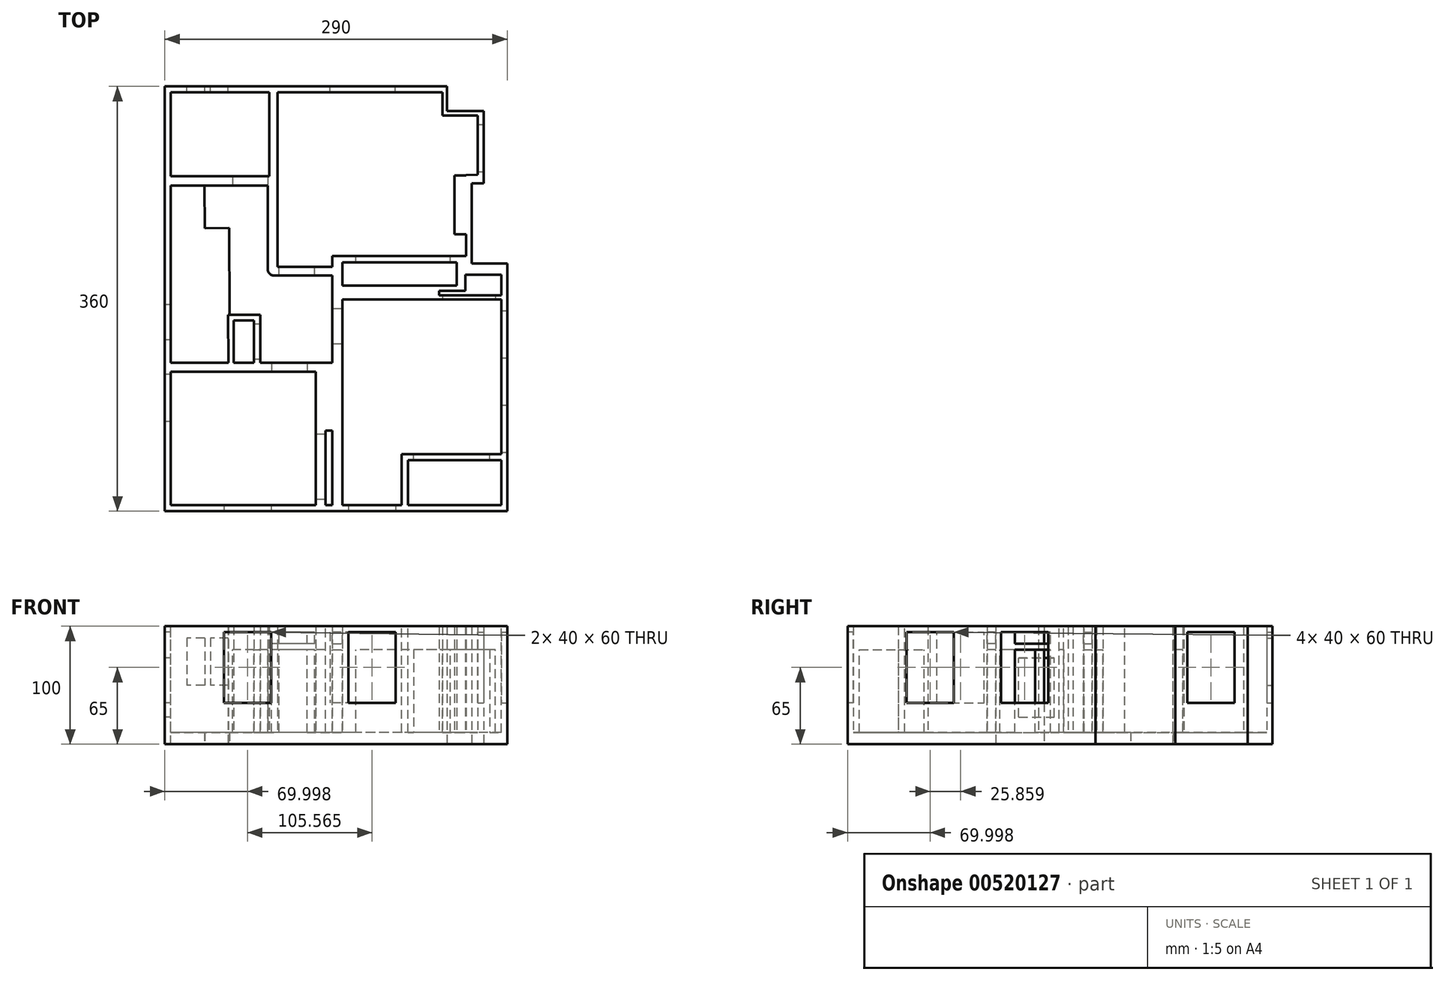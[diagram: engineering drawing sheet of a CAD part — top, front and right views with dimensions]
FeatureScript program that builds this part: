
annotation { "Feature Type Name" : "Feature", "Feature Type Description" : "" }
export const myFeature = defineFeature(function(context is Context, id is Id, definition is map)
    precondition{}
    {
        {
            var Q0;
            Q0=qCreatedBy(makeId("Top.planeOp"),FACE);
            var sketch = newSketch(context, id + "F0", { "sketchPlane" : qUnion([Q0])});
            skLineSegment(sketch, "E0.bottom", {"start": v(-136.75, 209.7) * mm, "end": v(93.5, 209.7) * mm});
            skLineSegment(sketch, "E0.top", {"start": v(-136.75, -140.3) * mm, "end": v(0, -140.3) * mm});
            skLineSegment(sketch, "E0.left", {"start": v(-136.75, 209.7) * mm, "end": v(-136.75, -20.3) * mm});
            skLineSegment(sketch, "E0.right", {"start": v(143.25, 59.7) * mm, "end": v(143.25, -140.3) * mm});
            skLineSegment(sketch, "E1", {"start": v(113.25, 59.7) * mm, "end": v(143.25, 59.7) * mm});
            skLineSegment(sketch, "E2", {"start": v(103.25, 89.37) * mm, "end": v(103.25, 139.37) * mm});
            skLineSegment(sketch, "E3", {"start": v(123.25, 139.7) * mm, "end": v(123.25, 190.05) * mm});
            skLineSegment(sketch, "E4", {"start": v(103.25, 139.37) * mm, "end": v(123.25, 139.7) * mm});
            skLineSegment(sketch, "E5", {"start": v(113.25, 59.7) * mm, "end": v(113.25, 139.54) * mm});
            skLineSegment(sketch, "E6", {"start": v(3.25, -140.3) * mm, "end": v(3.25, 69.7) * mm});
            skLineSegment(sketch, "E7", {"start": v(3.25, 69.7) * mm, "end": v(113.25, 69.7) * mm});
            skLineSegment(sketch, "E8", {"start": v(3.25, 39.7) * mm, "end": v(143.25, 39.7) * mm});
            skLineSegment(sketch, "E9", {"start": v(63.25, 69.7) * mm, "end": v(63.25, 39.7) * mm});
            skLineSegment(sketch, "E10", {"start": v(3.25, -20.3) * mm, "end": v(-136.75, -20.3) * mm});
            skLineSegment(sketch, "E11", {"start": v(-46.75, 59.7) * mm, "end": v(-46.75, 209.7) * mm});
            skLineSegment(sketch, "E12", {"start": v(-46.75, 59.7) * mm, "end": v(3.25, 59.7) * mm});
            skLineSegment(sketch, "E13", {"start": v(-136.75, 129.7) * mm, "end": v(-46.75, 129.7) * mm});
            skLineSegment(sketch, "E14", {"start": v(103.25, 89.37) * mm, "end": v(113.25, 89.37) * mm});
            skLineSegment(sketch, "E15", {"start": v(-80.56, 99.7) * mm, "end": v(-80.56, -20.3) * mm});
            skLineSegment(sketch, "E16", {"start": v(-80.56, 99.7) * mm, "end": v(-136.75, 99.7) * mm});
            skLineSegment(sketch, "E17", {"start": v(-141.75, 214.7) * mm, "end": v(-141.75, -145.77) * mm});
            skLineSegment(sketch, "E18", {"start": v(-141.75, -145.3) * mm, "end": v(148.25, -145.3) * mm});
            skLineSegment(sketch, "E19", {"start": v(148.25, -145.3) * mm, "end": v(148.25, 64.7) * mm});
            skLineSegment(sketch, "E20", {"start": v(148.25, 64.7) * mm, "end": v(118.25, 64.7) * mm});
            skLineSegment(sketch, "E21", {"start": v(118.25, 64.7) * mm, "end": v(118.25, 132.41) * mm});
            skLineSegment(sketch, "E22", {"start": v(118.25, 132.41) * mm, "end": v(128.25, 132.41) * mm});
            skLineSegment(sketch, "E23", {"start": v(128.25, 132.41) * mm, "end": v(128.25, 193.74) * mm});
            skLineSegment(sketch, "E24", {"start": v(97.29, 214.7) * mm, "end": v(-141.75, 214.7) * mm});
            skLineSegment(sketch, "E25", {"start": v(-136.75, 135.4) * mm, "end": v(-52.51, 135.4) * mm});
            skLineSegment(sketch, "E26", {"start": v(-52.51, 135.4) * mm, "end": v(-52.51, 209.7) * mm});
            skLineSegment(sketch, "E27", {"start": v(-53.07, 129.7) * mm, "end": v(-53.07, 59.7) * mm});
            skLineSegment(sketch, "E28", {"start": v(-53.07, 59.7) * mm, "end": v(-53.07, 54.34) * mm});
            skLineSegment(sketch, "E29", {"start": v(-53.07, 54.34) * mm, "end": v(3.25, 54.34) * mm});
            skLineSegment(sketch, "E30.bottom", {"start": v(5.65, 66.66) * mm, "end": v(60.34, 66.66) * mm});
            skLineSegment(sketch, "E30.top", {"start": v(5.65, 42.9) * mm, "end": v(60.34, 42.9) * mm});
            skLineSegment(sketch, "E30.left", {"start": v(5.65, 66.66) * mm, "end": v(5.65, 42.9) * mm});
            skLineSegment(sketch, "E30.right", {"start": v(60.34, 66.66) * mm, "end": v(60.34, 42.9) * mm});
            skLineSegment(sketch, "E31.bottom", {"start": v(-136.75, -24.43) * mm, "end": v(0, -24.43) * mm});
            skLineSegment(sketch, "E31.left", {"start": v(-136.75, -24.43) * mm, "end": v(-136.75, -140.3) * mm});
            skLineSegment(sketch, "E31.right", {"start": v(0, -24.43) * mm, "end": v(0, -134.7) * mm});
            skLineSegment(sketch, "E32.bottom", {"start": v(7.81, 34.85) * mm, "end": v(138.07, 34.85) * mm});
            skLineSegment(sketch, "E32.top", {"start": v(7.81, -134.7) * mm, "end": v(138.07, -134.7) * mm});
            skLineSegment(sketch, "E32.left", {"start": v(7.81, 34.85) * mm, "end": v(7.81, -134.7) * mm});
            skLineSegment(sketch, "E32.right", {"start": v(138.07, 34.85) * mm, "end": v(138.07, -134.7) * mm});
            skLineSegment(sketch, "E33", {"start": v(67.33, 44.96) * mm, "end": v(67.33, 65.85) * mm});
            skLineSegment(sketch, "E34", {"start": v(67.33, 65.85) * mm, "end": v(108.15, 65.85) * mm});
            skLineSegment(sketch, "E35", {"start": v(108.15, 65.85) * mm, "end": v(108.15, 55.21) * mm});
            skLineSegment(sketch, "E36", {"start": v(108.15, 55.21) * mm, "end": v(138.12, 55.21) * mm});
            skLineSegment(sketch, "E37", {"start": v(138.12, 55.21) * mm, "end": v(138.12, 44.96) * mm});
            skLineSegment(sketch, "E38", {"start": v(138.12, 44.96) * mm, "end": v(67.33, 44.96) * mm});
            skLineSegment(sketch, "E39", {"start": v(-136.75, 94.77) * mm, "end": v(-86.74, 94.77) * mm});
            skLineSegment(sketch, "E40", {"start": v(-86.74, 94.77) * mm, "end": v(-86.74, -20.3) * mm});
            skLineSegment(sketch, "E41", {"start": v(97.29, 214.7) * mm, "end": v(97.29, 193.74) * mm});
            skLineSegment(sketch, "E42", {"start": v(97.29, 193.74) * mm, "end": v(128.25, 193.74) * mm});
            skLineSegment(sketch, "E43", {"start": v(128.25, 193.74) * mm, "end": v(128.25, 190.05) * mm});
            skLineSegment(sketch, "E44", {"start": v(123.25, 190.05) * mm, "end": v(93.5, 190.05) * mm});
            skLineSegment(sketch, "E45", {"start": v(93.5, 190.05) * mm, "end": v(93.5, 209.7) * mm});
            skPoint(sketch, "E46.orphan", {"position": v(123.25, 209.7) * mm});
            skLineSegment(sketch, "E47", {"start": v(0, -134.7) * mm, "end": v(0, -140.3) * mm});
            skLineSegment(sketch, "E48.trimOffspring", {"start": v(3.25, -140.3) * mm, "end": v(143.25, -140.3) * mm});
            skSolve(sketch);
        }
        {
            var Q0;
            Q0=qCreatedBy(makeId("Top.planeOp"),FACE);
            var sketch = newSketch(context, id + "F1", { "sketchPlane" : qUnion([Q0])});
            skLineSegment(sketch, "E49", {"start": v(-53.18, 210.11) * mm, "end": v(-53.18, 138.73) * mm});
            skLineSegment(sketch, "E50", {"start": v(-53.18, 138.73) * mm, "end": v(-138.25, 138.73) * mm});
            skLineSegment(sketch, "E51", {"start": v(-138.25, 138.73) * mm, "end": v(-138.25, 130.57) * mm});
            skLineSegment(sketch, "E52", {"start": v(-138.25, 130.57) * mm, "end": v(-54.54, 130.57) * mm});
            skLineSegment(sketch, "E53", {"start": v(-54.54, 130.57) * mm, "end": v(-54.54, 54.42) * mm});
            skLineSegment(sketch, "E54", {"start": v(-54.54, 54.42) * mm, "end": v(0, 54.42) * mm});
            skLineSegment(sketch, "E55", {"start": v(0, 54.42) * mm, "end": v(0, -19.68) * mm});
            skLineSegment(sketch, "E56", {"start": v(0, -19.68) * mm, "end": v(-61, -19.68) * mm});
            skLineSegment(sketch, "E57", {"start": v(-137.2, -27.08) * mm, "end": v(-13.82, -27.08) * mm});
            skLineSegment(sketch, "E58", {"start": v(0, -143.06) * mm, "end": v(8.69, -143.06) * mm});
            skLineSegment(sketch, "E59", {"start": v(8.69, -143.06) * mm, "end": v(8.69, 34.03) * mm});
            skLineSegment(sketch, "E60", {"start": v(8.77, 45.73) * mm, "end": v(8.77, 65.56) * mm});
            skLineSegment(sketch, "E61", {"start": v(8.77, 65.56) * mm, "end": v(105.55, 65.56) * mm});
            skLineSegment(sketch, "E62", {"start": v(105.55, 65.56) * mm, "end": v(105.55, 55.1) * mm});
            skLineSegment(sketch, "E63", {"start": v(112.8, 55.1) * mm, "end": v(143.3, 55.1) * mm});
            skLineSegment(sketch, "E64", {"start": v(90.95, 65.56) * mm, "end": v(96.31, 65.56) * mm});
            skLineSegment(sketch, "E65", {"start": v(-53.18, 210.11) * mm, "end": v(-46.38, 210.11) * mm});
            skLineSegment(sketch, "E66", {"start": v(-46.38, 210.11) * mm, "end": v(-46.38, 61.89) * mm});
            skLineSegment(sketch, "E67", {"start": v(-46.38, 61.89) * mm, "end": v(0, 61.89) * mm});
            skLineSegment(sketch, "E68", {"start": v(0, 61.89) * mm, "end": v(0, 71.07) * mm});
            skLineSegment(sketch, "E69", {"start": v(0, 71.07) * mm, "end": v(114.87, 71.07) * mm});
            skLineSegment(sketch, "E70", {"start": v(114.87, 71.07) * mm, "end": v(114.87, 61.89) * mm});
            skLineSegment(sketch, "E71", {"start": v(114.87, 61.89) * mm, "end": v(144.27, 61.89) * mm});
            skLineSegment(sketch, "E72", {"start": v(144.27, 61.89) * mm, "end": v(143.3, 55.1) * mm});
            skLineSegment(sketch, "E73", {"start": v(113.41, 89.48) * mm, "end": v(103.62, 89.48) * mm});
            skLineSegment(sketch, "E74", {"start": v(103.62, 89.48) * mm, "end": v(103.62, 139.21) * mm});
            skLineSegment(sketch, "E75", {"start": v(103.62, 139.21) * mm, "end": v(113.8, 139.21) * mm});
            skLineSegment(sketch, "E76", {"start": v(113.8, 139.21) * mm, "end": v(113.41, 89.48) * mm});
            skLineSegment(sketch, "E77", {"start": v(-87.85, -19.68) * mm, "end": v(-137.24, -19.68) * mm});
            skLineSegment(sketch, "E78", {"start": v(-137.24, -19.68) * mm, "end": v(-137.2, -27.08) * mm});
            skLineSegment(sketch, "E79", {"start": v(138, 55.1) * mm, "end": v(143.3, 55.1) * mm});
            skLineSegment(sketch, "E80", {"start": v(105.55, 55.1) * mm, "end": v(105.55, 45.73) * mm});
            skLineSegment(sketch, "E81", {"start": v(8.77, 45.73) * mm, "end": v(105.55, 45.73) * mm});
            skLineSegment(sketch, "E82", {"start": v(8.69, 34.03) * mm, "end": v(90.67, 34.03) * mm});
            skLineSegment(sketch, "E83", {"start": v(90.67, 37.73) * mm, "end": v(90.67, 41.44) * mm});
            skLineSegment(sketch, "E84", {"start": v(90.67, 41.44) * mm, "end": v(112.8, 41.44) * mm});
            skLineSegment(sketch, "E85", {"start": v(112.8, 41.44) * mm, "end": v(112.8, 55.1) * mm});
            skLineSegment(sketch, "E86", {"start": v(112.8, 55.1) * mm, "end": v(112.8, 55.1) * mm});
            skPoint(sketch, "E87.orphan", {"position": v(0, -27.08) * mm});
            skLineSegment(sketch, "E88", {"start": v(-13.82, -27.08) * mm, "end": v(-13.82, -77.07) * mm});
            skLineSegment(sketch, "E89", {"start": v(-5.52, -77.07) * mm, "end": v(0, -77.07) * mm});
            skLineSegment(sketch, "E90", {"start": v(0, -77.07) * mm, "end": v(0, -143.06) * mm});
            skLineSegment(sketch, "E91", {"start": v(90.67, 34.03) * mm, "end": v(145.65, 34.03) * mm});
            skLineSegment(sketch, "E92", {"start": v(90.67, 37.73) * mm, "end": v(145.65, 37.73) * mm});
            skLineSegment(sketch, "E93", {"start": v(145.65, 37.73) * mm, "end": v(145.65, 34.03) * mm});
            skLineSegment(sketch, "E94", {"start": v(-13.82, -77.07) * mm, "end": v(-13.82, -142.7) * mm});
            skLineSegment(sketch, "E95", {"start": v(-13.82, -142.7) * mm, "end": v(-5.52, -142.7) * mm});
            skLineSegment(sketch, "E96", {"start": v(-5.52, -142.7) * mm, "end": v(-5.52, -77.07) * mm});
            skLineSegment(sketch, "E97", {"start": v(58.82, -141.74) * mm, "end": v(58.82, -96.98) * mm});
            skLineSegment(sketch, "E98", {"start": v(58.82, -96.98) * mm, "end": v(144.68, -96.98) * mm});
            skLineSegment(sketch, "E99", {"start": v(64.28, -141.74) * mm, "end": v(64.28, -102.13) * mm});
            skLineSegment(sketch, "E100", {"start": v(58.82, -141.74) * mm, "end": v(64.28, -141.74) * mm});
            skLineSegment(sketch, "E101", {"start": v(144.68, -96.98) * mm, "end": v(144.68, -102.13) * mm});
            skLineSegment(sketch, "E102", {"start": v(144.68, -102.13) * mm, "end": v(64.28, -102.13) * mm});
            skLineSegment(sketch, "E103.bottom", {"start": v(93.55, 212.13) * mm, "end": v(97.19, 212.13) * mm});
            skLineSegment(sketch, "E103.top", {"start": v(93.55, 190.13) * mm, "end": v(124.8, 190.13) * mm});
            skLineSegment(sketch, "E103.left", {"start": v(93.55, 212.13) * mm, "end": v(93.55, 190.13) * mm});
            skLineSegment(sketch, "E103.right", {"start": v(124.8, 193.53) * mm, "end": v(124.8, 190.13) * mm});
            skLineSegment(sketch, "E104", {"start": v(97.19, 212.13) * mm, "end": v(97.19, 193.53) * mm});
            skLineSegment(sketch, "E105", {"start": v(97.19, 193.53) * mm, "end": v(124.8, 193.53) * mm});
            skLineSegment(sketch, "E106", {"start": v(-61, -19.68) * mm, "end": v(-61, 21.1) * mm});
            skLineSegment(sketch, "E107", {"start": v(-61, 21.1) * mm, "end": v(-88.21, 21.1) * mm});
            skLineSegment(sketch, "E108", {"start": v(-88.21, 21.1) * mm, "end": v(-87.85, -19.68) * mm});
            skLineSegment(sketch, "E109.bottom", {"start": v(-83.58, 16.47) * mm, "end": v(-66.22, 16.47) * mm});
            skLineSegment(sketch, "E109.top", {"start": v(-83.58, -19.68) * mm, "end": v(-66.22, -19.68) * mm});
            skLineSegment(sketch, "E109.left", {"start": v(-83.58, 16.47) * mm, "end": v(-83.58, -19.68) * mm});
            skLineSegment(sketch, "E109.right", {"start": v(-66.22, 16.47) * mm, "end": v(-66.22, -19.68) * mm});
            skSolve(sketch);
        }
        {
            var Q0;
            Q0=qCreatedBy(makeId("Top.planeOp"),FACE);
            var sketch = newSketch(context, id + "F2", { "sketchPlane" : qUnion([Q0])});
            skLineSegment(sketch, "E110", {"start": v(-138.73, 211.72) * mm, "end": v(95.24, 211.72) * mm});
            skLineSegment(sketch, "E111", {"start": v(124.93, 192.2) * mm, "end": v(124.93, 138.77) * mm});
            skLineSegment(sketch, "E112", {"start": v(124.93, 138.77) * mm, "end": v(113.56, 138.77) * mm});
            skLineSegment(sketch, "E113", {"start": v(113.56, 138.77) * mm, "end": v(113.56, 61.87) * mm});
            skLineSegment(sketch, "E114", {"start": v(113.56, 61.87) * mm, "end": v(144.48, 61.87) * mm});
            skLineSegment(sketch, "E115", {"start": v(144.48, 61.87) * mm, "end": v(144.48, -142.02) * mm});
            skLineSegment(sketch, "E116", {"start": v(144.48, -142.02) * mm, "end": v(-137.63, -142.02) * mm});
            skLineSegment(sketch, "E117", {"start": v(-137.3, -85.55) * mm, "end": v(-137.61, -19.93) * mm});
            skLineSegment(sketch, "E118", {"start": v(-87.17, 94.65) * mm, "end": v(-86.91, -19.68) * mm});
            skLineSegment(sketch, "E119", {"start": v(-86.91, -19.68) * mm, "end": v(-137.61, -19.93) * mm});
            skLineSegment(sketch, "E120.trimOffspring", {"start": v(-138.34, 131.48) * mm, "end": v(-138.73, 211.72) * mm});
            skLineSegment(sketch, "E121", {"start": v(-87.17, 94.65) * mm, "end": v(-108.05, 94.6) * mm});
            skLineSegment(sketch, "E122", {"start": v(-108.05, 94.6) * mm, "end": v(-108.13, 131.48) * mm});
            skLineSegment(sketch, "E123", {"start": v(-108.13, 131.48) * mm, "end": v(-138.34, 131.48) * mm});
            skLineSegment(sketch, "E124", {"start": v(-137.9, -85.55) * mm, "end": v(-137.3, -85.55) * mm});
            skLineSegment(sketch, "E125", {"start": v(-137.9, -85.55) * mm, "end": v(-137.63, -142.02) * mm});
            skLineSegment(sketch, "E126", {"start": v(95.24, 211.72) * mm, "end": v(95.24, 192.2) * mm});
            skLineSegment(sketch, "E127", {"start": v(95.24, 192.2) * mm, "end": v(124.93, 192.2) * mm});
            skSolve(sketch);
        }
        {
            var Q0;
            Q0 = qSketchRegion(id + "F2", true);
            extrude(context, id + "F3", {"entities" : qUnion([Q0]), "depth" : 10 * mm, "offsetDistance" : 25 * mm});
        }
        {
            var Q0;
            Q0 = qSketchRegion(id + "F0", true);
            extrude(context, id + "F4", {"entities" : qUnion([Q0]), "operationType" : NewBodyOperationType.ADD, "depth" : 100 * mm, "offsetDistance" : 25 * mm});
        }
        {
            var Q0;
            Q0 = qSketchRegion(id + "F1", true);
            extrude(context, id + "F5", {"entities" : qUnion([Q0]), "operationType" : NewBodyOperationType.ADD, "depth" : 100 * mm, "offsetDistance" : 25 * mm});
        }
        {
            var Q0;
            Q0=makeQuery(id+"F4.opExtrude","SWEPT_FACE",FACE,{"disambiguationData":[OSD([sQuery(id+"F0.wireOp",EDGE,"E19")])]});
            var sketch = newSketch(context, id + "F6", { "sketchPlane" : qUnion([Q0])});
            skPoint(sketch, "E128.oppositeSnap0", {"position": v(-19.27, 35) * mm});
            skLineSegment(sketch, "E128.bottom", {"start": v(-95.3, 95) * mm, "end": v(-55.3, 95) * mm});
            skLineSegment(sketch, "E128.top", {"start": v(-95.3, 35) * mm, "end": v(-55.3, 35) * mm});
            skLineSegment(sketch, "E128.left", {"start": v(-95.3, 95) * mm, "end": v(-95.3, 35) * mm});
            skLineSegment(sketch, "E128.right", {"start": v(-55.3, 95) * mm, "end": v(-55.3, 35) * mm});
            skLineSegment(sketch, "E129.bottom", {"start": v(-15.3, 95) * mm, "end": v(24.7, 95) * mm});
            skLineSegment(sketch, "E129.top", {"start": v(-15.3, 35) * mm, "end": v(24.7, 35) * mm});
            skLineSegment(sketch, "E129.left", {"start": v(-15.3, 95) * mm, "end": v(-15.3, 35) * mm});
            skLineSegment(sketch, "E129.right", {"start": v(24.7, 95) * mm, "end": v(24.7, 35) * mm});
            skSolve(sketch);
        }
        {
            var Q0;
            Q0 = qSketchRegion(id + "F6", true);
            extrude(context, id + "F7", {"entities" : qUnion([Q0]), "operationType" : NewBodyOperationType.REMOVE, "oppositeDirection" : true, "depth" : 10 * mm, "offsetDistance" : 25 * mm});
        }
        {
            var Q0;
            Q0=makeQuery(id+"F4.opExtrude","SWEPT_FACE",FACE,{"disambiguationData":[OSD([sQuery(id+"F0.wireOp",EDGE,"E23")])]});
            var sketch = newSketch(context, id + "F8", { "sketchPlane" : qUnion([Q0])});
            skLineSegment(sketch, "E130.bottom", {"start": v(142.41, 95) * mm, "end": v(182.41, 95) * mm});
            skLineSegment(sketch, "E130.top", {"start": v(142.41, 35) * mm, "end": v(182.41, 35) * mm});
            skLineSegment(sketch, "E130.left", {"start": v(142.41, 95) * mm, "end": v(142.41, 35) * mm});
            skLineSegment(sketch, "E130.right", {"start": v(182.41, 95) * mm, "end": v(182.41, 35) * mm});
            skSolve(sketch);
        }
        {
            var Q0;
            Q0 = qSketchRegion(id + "F8", true);
            extrude(context, id + "F9", {"entities" : qUnion([Q0]), "operationType" : NewBodyOperationType.REMOVE, "oppositeDirection" : true, "depth" : 10 * mm, "offsetDistance" : 25 * mm});
        }
        {
            var Q0;
            Q0=makeQuery(id+"F4.opExtrude","SWEPT_FACE",FACE,{"disambiguationData":[OSD([sQuery(id+"F0.wireOp",EDGE,"E18")])]});
            var sketch = newSketch(context, id + "F10", { "sketchPlane" : qUnion([Q0])});
            skLineSegment(sketch, "E131.bottom", {"start": v(13.81, 95) * mm, "end": v(53.81, 95) * mm});
            skLineSegment(sketch, "E131.top", {"start": v(13.81, 35) * mm, "end": v(53.81, 35) * mm});
            skLineSegment(sketch, "E131.left", {"start": v(13.81, 95) * mm, "end": v(13.81, 35) * mm});
            skLineSegment(sketch, "E131.right", {"start": v(53.81, 95) * mm, "end": v(53.81, 35) * mm});
            skLineSegment(sketch, "E132.bottom", {"start": v(-91.75, 95) * mm, "end": v(-51.75, 95) * mm});
            skLineSegment(sketch, "E132.top", {"start": v(-91.75, 35) * mm, "end": v(-51.75, 35) * mm});
            skLineSegment(sketch, "E132.left", {"start": v(-91.75, 95) * mm, "end": v(-91.75, 35) * mm});
            skLineSegment(sketch, "E132.right", {"start": v(-51.75, 95) * mm, "end": v(-51.75, 35) * mm});
            skSolve(sketch);
        }
        {
            var Q0;
            Q0 = qSketchRegion(id + "F10", true);
            extrude(context, id + "F11", {"entities" : qUnion([Q0]), "operationType" : NewBodyOperationType.REMOVE, "oppositeDirection" : true, "depth" : 10 * mm, "offsetDistance" : 25 * mm});
        }
        {
            var Q0;
            Q0=makeQuery(id+"F4.opExtrude","SWEPT_FACE",FACE,{"disambiguationData":[OSD([sQuery(id+"F0.wireOp",EDGE,"E17")])]});
            var sketch = newSketch(context, id + "F12", { "sketchPlane" : qUnion([Q0])});
            skLineSegment(sketch, "E133.bottom", {"start": v(29.43, 95) * mm, "end": v(69.43, 95) * mm});
            skLineSegment(sketch, "E133.top", {"start": v(29.43, 35) * mm, "end": v(69.43, 35) * mm});
            skLineSegment(sketch, "E133.left", {"start": v(29.43, 95) * mm, "end": v(29.43, 35) * mm});
            skLineSegment(sketch, "E133.right", {"start": v(69.43, 95) * mm, "end": v(69.43, 35) * mm});
            skLineSegment(sketch, "E134.bottom", {"start": v(-29.7, 73) * mm, "end": v(0.3, 73) * mm});
            skLineSegment(sketch, "E134.top", {"start": v(-29.7, 23) * mm, "end": v(0.3, 23) * mm});
            skLineSegment(sketch, "E134.left", {"start": v(-29.7, 73) * mm, "end": v(-29.7, 23) * mm});
            skLineSegment(sketch, "E134.right", {"start": v(0.3, 73) * mm, "end": v(0.3, 23) * mm});
            skSolve(sketch);
        }
        {
            var Q0;
            Q0 = qSketchRegion(id + "F12", true);
            extrude(context, id + "F13", {"entities" : qUnion([Q0]), "operationType" : NewBodyOperationType.REMOVE, "oppositeDirection" : true, "depth" : 10 * mm, "offsetDistance" : 25 * mm});
        }
        {
            var Q0;
            Q0=makeQuery(id+"F4.opExtrude","SWEPT_FACE",FACE,{"disambiguationData":[OSD([sQuery(id+"F0.wireOp",EDGE,"E24")])]});
            var sketch = newSketch(context, id + "F14", { "sketchPlane" : qUnion([Q0])});
            skLineSegment(sketch, "E135.bottom", {"start": v(88.07, 90) * mm, "end": v(103.07, 90) * mm});
            skLineSegment(sketch, "E135.top", {"start": v(88.07, 50) * mm, "end": v(103.07, 50) * mm});
            skLineSegment(sketch, "E135.left", {"start": v(88.07, 90) * mm, "end": v(88.07, 50) * mm});
            skLineSegment(sketch, "E135.right", {"start": v(103.07, 90) * mm, "end": v(103.07, 50) * mm});
            skLineSegment(sketch, "E136.bottom", {"start": v(108.07, 90) * mm, "end": v(123.07, 90) * mm});
            skLineSegment(sketch, "E136.top", {"start": v(108.07, 50) * mm, "end": v(123.07, 50) * mm});
            skLineSegment(sketch, "E136.left", {"start": v(108.07, 90) * mm, "end": v(108.07, 50) * mm});
            skLineSegment(sketch, "E136.right", {"start": v(123.07, 90) * mm, "end": v(123.07, 50) * mm});
            skLineSegment(sketch, "E137.bottom", {"start": v(-53.25, 95) * mm, "end": v(1.75, 95) * mm});
            skLineSegment(sketch, "E137.top", {"start": v(-53.25, 35) * mm, "end": v(1.75, 35) * mm});
            skLineSegment(sketch, "E137.left", {"start": v(-53.25, 95) * mm, "end": v(-53.25, 35) * mm});
            skLineSegment(sketch, "E137.right", {"start": v(1.75, 95) * mm, "end": v(1.75, 35) * mm});
            skSolve(sketch);
        }
        {
            var Q0;
            Q0 = qSketchRegion(id + "F14", true);
            extrude(context, id + "F15", {"entities" : qUnion([Q0]), "operationType" : NewBodyOperationType.REMOVE, "oppositeDirection" : true, "depth" : 10 * mm, "offsetDistance" : 25 * mm});
        }
        {
            var Q0;
            Q0=makeQuery(id+"F5.opExtrude","SWEPT_FACE",FACE,{"disambiguationData":[OSD([sQuery(id+"F1.wireOp",EDGE,"E69")])]});
            var sketch = newSketch(context, id + "F16", { "sketchPlane" : qUnion([Q0])});
            skLineSegment(sketch, "E138.bottom", {"start": v(-100, 10) * mm, "end": v(-20, 10) * mm});
            skLineSegment(sketch, "E138.top", {"start": v(-100, 80) * mm, "end": v(-20, 80) * mm});
            skLineSegment(sketch, "E138.left", {"start": v(-100, 10) * mm, "end": v(-100, 80) * mm});
            skLineSegment(sketch, "E138.right", {"start": v(-20, 10) * mm, "end": v(-20, 80) * mm});
            skSolve(sketch);
        }
        {
            var Q0;
            Q0 = qSketchRegion(id + "F16", true);
            extrude(context, id + "F17", {"entities" : qUnion([Q0]), "operationType" : NewBodyOperationType.REMOVE, "oppositeDirection" : true, "depth" : 10 * mm, "offsetDistance" : 25 * mm});
        }
        {
            var Q0;
            Q0=makeQuery(id+"F5.opExtrude","SWEPT_FACE",FACE,{"disambiguationData":[OSD([sQuery(id+"F1.wireOp",EDGE,"E67")])]});
            var sketch = newSketch(context, id + "F18", { "sketchPlane" : qUnion([Q0])});
            skLineSegment(sketch, "E139.bottom", {"start": v(15, 10) * mm, "end": v(45, 10) * mm});
            skLineSegment(sketch, "E139.top", {"start": v(15, 80) * mm, "end": v(45, 80) * mm});
            skLineSegment(sketch, "E139.left", {"start": v(15, 10) * mm, "end": v(15, 80) * mm});
            skLineSegment(sketch, "E139.right", {"start": v(45, 10) * mm, "end": v(45, 80) * mm});
            skLineSegment(sketch, "E140.bottom", {"start": v(15, 85) * mm, "end": v(45, 85) * mm});
            skLineSegment(sketch, "E140.top", {"start": v(15, 95) * mm, "end": v(45, 95) * mm});
            skLineSegment(sketch, "E140.left", {"start": v(15, 85) * mm, "end": v(15, 95) * mm});
            skLineSegment(sketch, "E140.right", {"start": v(45, 85) * mm, "end": v(45, 95) * mm});
            skSolve(sketch);
        }
        {
            var Q0;
            Q0 = qSketchRegion(id + "F18", true);
            extrude(context, id + "F19", {"entities" : qUnion([Q0]), "operationType" : NewBodyOperationType.REMOVE, "oppositeDirection" : true, "depth" : 10 * mm, "offsetDistance" : 25 * mm});
        }
        {
            var Q0;
            Q0=makeQuery(id+"F5.opExtrude","SWEPT_FACE",FACE,{"disambiguationData":[OSD([sQuery(id+"F1.wireOp",EDGE,"E57")])]});
            var sketch = newSketch(context, id + "F20", { "sketchPlane" : qUnion([Q0])});
            skLineSegment(sketch, "E141.bottom", {"start": v(-21.32, 10) * mm, "end": v(-51.32, 10) * mm});
            skLineSegment(sketch, "E141.top", {"start": v(-21.32, 80) * mm, "end": v(-51.32, 80) * mm});
            skLineSegment(sketch, "E141.left", {"start": v(-21.32, 10) * mm, "end": v(-21.32, 80) * mm});
            skLineSegment(sketch, "E141.right", {"start": v(-51.32, 10) * mm, "end": v(-51.32, 80) * mm});
            skLineSegment(sketch, "E142.bottom", {"start": v(-21.32, 85) * mm, "end": v(-51.32, 85) * mm});
            skLineSegment(sketch, "E142.top", {"start": v(-21.32, 95) * mm, "end": v(-51.32, 95) * mm});
            skLineSegment(sketch, "E142.left", {"start": v(-21.32, 85) * mm, "end": v(-21.32, 95) * mm});
            skLineSegment(sketch, "E142.right", {"start": v(-51.32, 85) * mm, "end": v(-51.32, 95) * mm});
            skSolve(sketch);
        }
        {
            var Q0;
            Q0 = qSketchRegion(id + "F20", true);
            extrude(context, id + "F21", {"entities" : qUnion([Q0]), "operationType" : NewBodyOperationType.REMOVE, "oppositeDirection" : true, "depth" : 10 * mm, "offsetDistance" : 25 * mm});
        }
        {
            var Q0;
            Q0=makeQuery(id+"F5.opExtrude","SWEPT_FACE",FACE,{"disambiguationData":[OSD([sQuery(id+"F1.wireOp",EDGE,"E59")])]});
            var sketch = newSketch(context, id + "F22", { "sketchPlane" : qUnion([Q0])});
            skLineSegment(sketch, "E143.bottom", {"start": v(26.53, 10) * mm, "end": v(-3.47, 10) * mm});
            skLineSegment(sketch, "E143.top", {"start": v(26.53, 80) * mm, "end": v(-3.47, 80) * mm});
            skLineSegment(sketch, "E143.left", {"start": v(26.53, 10) * mm, "end": v(26.53, 80) * mm});
            skLineSegment(sketch, "E143.right", {"start": v(-3.47, 10) * mm, "end": v(-3.47, 80) * mm});
            skLineSegment(sketch, "E144.bottom", {"start": v(26.53, 85) * mm, "end": v(-3.47, 85) * mm});
            skLineSegment(sketch, "E144.top", {"start": v(26.53, 95) * mm, "end": v(-3.47, 95) * mm});
            skLineSegment(sketch, "E144.left", {"start": v(26.53, 85) * mm, "end": v(26.53, 95) * mm});
            skLineSegment(sketch, "E144.right", {"start": v(-3.47, 85) * mm, "end": v(-3.47, 95) * mm});
            skSolve(sketch);
        }
        {
            var Q0;
            Q0 = qSketchRegion(id + "F22", true);
            extrude(context, id + "F23", {"entities" : qUnion([Q0]), "operationType" : NewBodyOperationType.REMOVE, "oppositeDirection" : true, "depth" : 10 * mm, "offsetDistance" : 25 * mm});
        }
        {
            var Q0;
            Q0=makeQuery(id+"F5.opExtrude","SWEPT_FACE",FACE,{"disambiguationData":[OSD([sQuery(id+"F1.wireOp",EDGE,"E52")])]});
            var sketch = newSketch(context, id + "F24", { "sketchPlane" : qUnion([Q0])});
            skLineSegment(sketch, "E145.bottom", {"start": v(-54.53, 10) * mm, "end": v(-84.53, 10) * mm});
            skLineSegment(sketch, "E145.top", {"start": v(-54.53, 80) * mm, "end": v(-84.53, 80) * mm});
            skLineSegment(sketch, "E145.left", {"start": v(-54.53, 10) * mm, "end": v(-54.53, 80) * mm});
            skLineSegment(sketch, "E145.right", {"start": v(-84.53, 10) * mm, "end": v(-84.53, 80) * mm});
            skSolve(sketch);
        }
        {
            var Q0;
            Q0 = qSketchRegion(id + "F24", true);
            extrude(context, id + "F25", {"entities" : qUnion([Q0]), "operationType" : NewBodyOperationType.REMOVE, "oppositeDirection" : true, "depth" : 10 * mm, "offsetDistance" : 25 * mm});
        }
        {
            var Q0;
            Q0=makeQuery(id+"F5.opExtrude","SWEPT_EDGE",EDGE,{"disambiguationData":[OSD([sQuery(id+"F1.wireOp",EDGE,"E53"),sQuery(id+"F1.wireOp",EDGE,"E54")])]});
            fillet(context, id + "F26", {"entities" : qUnion([Q0]), "radius" : 5 * mm, "tangentPropagation" : true, "allowEdgeOverflow" : false});
        }
        {
            var Q0;
            Q0=makeQuery(id+"F5.opExtrude","SWEPT_FACE",FACE,{"disambiguationData":[OSD([sQuery(id+"F1.wireOp",EDGE,"E82"),sQuery(id+"F1.wireOp",EDGE,"E91")])]});
            var sketch = newSketch(context, id + "F27", { "sketchPlane" : qUnion([Q0])});
            skLineSegment(sketch, "E146.bottom", {"start": v(138.25, 10) * mm, "end": v(93.25, 10) * mm});
            skLineSegment(sketch, "E146.top", {"start": v(138.25, 80) * mm, "end": v(93.25, 80) * mm});
            skLineSegment(sketch, "E146.left", {"start": v(138.25, 10) * mm, "end": v(138.25, 80) * mm});
            skLineSegment(sketch, "E146.right", {"start": v(93.25, 10) * mm, "end": v(93.25, 80) * mm});
            skSolve(sketch);
        }
        {
            var Q0;
            Q0 = qSketchRegion(id + "F27", true);
            extrude(context, id + "F28", {"entities" : qUnion([Q0]), "operationType" : NewBodyOperationType.REMOVE, "oppositeDirection" : true, "depth" : 5.6 * mm, "offsetDistance" : 25 * mm});
        }
        {
            var Q0;
            Q0=makeQuery(id+"F5.opExtrude","SWEPT_FACE",FACE,{"disambiguationData":[OSD([sQuery(id+"F1.wireOp",EDGE,"E88"),sQuery(id+"F1.wireOp",EDGE,"E94")])]});
            var sketch = newSketch(context, id + "F29", { "sketchPlane" : qUnion([Q0])});
            skLineSegment(sketch, "E147.bottom", {"start": v(135.3, 10) * mm, "end": v(80.3, 10) * mm});
            skLineSegment(sketch, "E147.top", {"start": v(135.3, 80) * mm, "end": v(80.3, 80) * mm});
            skLineSegment(sketch, "E147.left", {"start": v(135.3, 10) * mm, "end": v(135.3, 80) * mm});
            skLineSegment(sketch, "E147.right", {"start": v(80.3, 10) * mm, "end": v(80.3, 80) * mm});
            skSolve(sketch);
        }
        {
            var Q0;
            Q0 = qSketchRegion(id + "F29", true);
            extrude(context, id + "F30", {"entities" : qUnion([Q0]), "operationType" : NewBodyOperationType.REMOVE, "oppositeDirection" : true, "depth" : 8 * mm, "offsetDistance" : 25 * mm});
        }
        {
            var Q0;
            Q0=makeQuery(id+"F5.opExtrude","SWEPT_FACE",FACE,{"disambiguationData":[OSD([sQuery(id+"F1.wireOp",EDGE,"E98")])]});
            var sketch = newSketch(context, id + "F31", { "sketchPlane" : qUnion([Q0])});
            skLineSegment(sketch, "E148.bottom", {"start": v(-68.82, 10) * mm, "end": v(-133.25, 10) * mm});
            skLineSegment(sketch, "E148.top", {"start": v(-68.82, 80) * mm, "end": v(-133.25, 80) * mm});
            skLineSegment(sketch, "E148.left", {"start": v(-68.82, 10) * mm, "end": v(-68.82, 80) * mm});
            skLineSegment(sketch, "E148.right", {"start": v(-133.25, 10) * mm, "end": v(-133.25, 80) * mm});
            skSolve(sketch);
        }
        {
            var Q0;
            Q0 = qSketchRegion(id + "F31", true);
            extrude(context, id + "F32", {"entities" : qUnion([Q0]), "operationType" : NewBodyOperationType.REMOVE, "oppositeDirection" : true, "depth" : 10 * mm, "offsetDistance" : 25 * mm});
        }
        {
            var Q0;
            Q0=makeQuery(id+"F5.opExtrude","SWEPT_FACE",FACE,{"disambiguationData":[OSD([sQuery(id+"F1.wireOp",EDGE,"E106")])]});
            var sketch = newSketch(context, id + "F33", { "sketchPlane" : qUnion([Q0])});
            skLineSegment(sketch, "E149.bottom", {"start": v(13.6, 10) * mm, "end": v(-16.4, 10) * mm});
            skLineSegment(sketch, "E149.top", {"start": v(13.6, 80) * mm, "end": v(-16.4, 80) * mm});
            skLineSegment(sketch, "E149.left", {"start": v(13.6, 10) * mm, "end": v(13.6, 80) * mm});
            skLineSegment(sketch, "E149.right", {"start": v(-16.4, 10) * mm, "end": v(-16.4, 80) * mm});
            skSolve(sketch);
        }
        {
            var Q0;
            Q0 = qSketchRegion(id + "F33", true);
            extrude(context, id + "F34", {"entities" : qUnion([Q0]), "operationType" : NewBodyOperationType.REMOVE, "oppositeDirection" : true, "depth" : 10 * mm, "offsetDistance" : 25 * mm});
        }
    });
